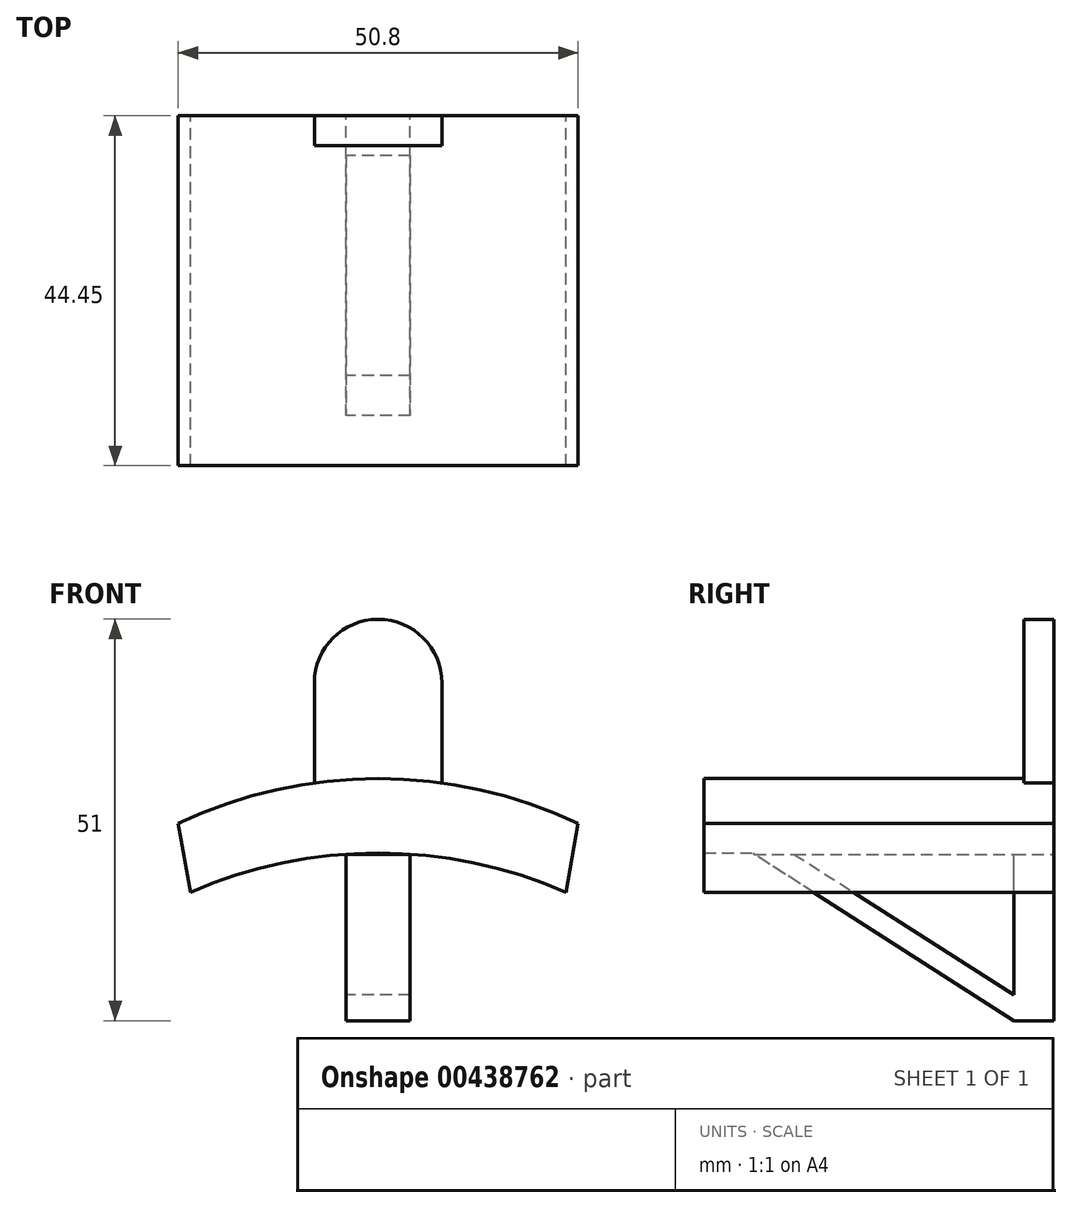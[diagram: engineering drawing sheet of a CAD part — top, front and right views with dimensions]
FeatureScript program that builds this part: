
annotation { "Feature Type Name" : "Feature", "Feature Type Description" : "" }
export const myFeature = defineFeature(function(context is Context, id is Id, definition is map)
    precondition{}
    {
        {
            var Q0;
            Q0=qCreatedBy(makeId("Front.planeOp"),FACE);
            var sketch = newSketch(context, id + "F0", { "sketchPlane" : qUnion([Q0])});
            skCircle(sketch, "E0", {"center": v(0, 0) * mm, "radius": 25.4 * mm, "construction": true});
            skArc(sketch, "E1", {"start": v(25.4, 0) * mm, "mid": v(0, 5.67) * mm, "end": v(-25.4, 0) * mm});
            skArc(sketch, "E2", {"start": v(23.84, -8.75) * mm, "mid": v(0, -3.78) * mm, "end": v(-23.84, -8.75) * mm});
            skLineSegment(sketch, "E3", {"start": v(-25.4, 0) * mm, "end": v(-23.84, -8.75) * mm});
            skLineSegment(sketch, "E4", {"start": v(25.4, 0) * mm, "end": v(23.84, -8.75) * mm});
            skLineSegment(sketch, "E5", {"start": v(-8.1, 5.12) * mm, "end": v(-8.1, 17.82) * mm});
            skLineSegment(sketch, "E6.MirrorCS", {"start": v(8.1, 5.12) * mm, "end": v(8.1, 17.82) * mm});
            skArc(sketch, "E7", {"start": v(8.1, 17.82) * mm, "mid": v(0, 25.93) * mm, "end": v(-8.1, 17.82) * mm});
            skLineSegment(sketch, "E8", {"start": v(-4.06, -3.92) * mm, "end": v(-4.06, -25.07) * mm});
            skLineSegment(sketch, "E9", {"start": v(-4.06, -25.07) * mm, "end": v(0, -25.07) * mm});
            skLineSegment(sketch, "E10.MirrorCS", {"start": v(4.06, -3.92) * mm, "end": v(4.06, -25.07) * mm});
            skLineSegment(sketch, "E11.MirrorCS", {"start": v(4.06, -25.07) * mm, "end": v(0, -25.07) * mm});
            skSolve(sketch);
        }
        {
            var Q0;
            {var subQ3=sQuery(id+"F0.wireOp",EDGE,"E3");Q0=makeQuery(id+"F0.imprint","IMPRINT",FACE,{"disambiguationData":[TD([[makeQuery(id+"F0.imprint","IMPRINT",EDGE,{"derivedFrom":subQ3}),1.0]])]});}
            extrude(context, id + "F1", {"entities" : qUnion([Q0]), "depth" : 44.45 * mm});
        }
        {
            var Q0;
            {var subQ0=sQuery(id+"F0.wireOp",EDGE,"E5");Q0=makeQuery(id+"F0.imprint","IMPRINT",FACE,{"disambiguationData":[TD([[makeQuery(id+"F0.imprint","IMPRINT",EDGE,{"derivedFrom":subQ0}),-1.0]])]});}
            extrude(context, id + "F2", {"entities" : qUnion([Q0]), "operationType" : NewBodyOperationType.ADD, "depth" : 3.8 * mm});
        }
        {
            var Q0;
            {var subQ1=sQuery(id+"F0.wireOp",EDGE,"E8");Q0=makeQuery(id+"F0.imprint","IMPRINT",FACE,{"disambiguationData":[TD([[makeQuery(id+"F0.imprint","IMPRINT",EDGE,{"derivedFrom":subQ1}),1.0]])]});}
            extrude(context, id + "F3", {"entities" : qUnion([Q0]), "operationType" : NewBodyOperationType.ADD, "depth" : 38.1 * mm});
        }
        {
            var Q0;
            Q0=makeQuery(id+"F3.opExtrude","SWEPT_FACE",FACE,{"disambiguationData":[OSD([sQuery(id+"F0.wireOp",EDGE,"E8")])]});
            var sketch = newSketch(context, id + "F4", { "sketchPlane" : qUnion([Q0])});
            skLineSegment(sketch, "E12", {"start": v(0, -3.92) * mm, "end": v(0, -25.07) * mm});
            skLineSegment(sketch, "E13", {"start": v(0, -25.07) * mm, "end": v(5.08, -25.07) * mm});
            skLineSegment(sketch, "E14", {"start": v(5.08, -25.07) * mm, "end": v(38.1, -3.92) * mm});
            skLineSegment(sketch, "E15", {"start": v(33.02, -3.92) * mm, "end": v(0, -25.07) * mm});
            skLineSegment(sketch, "E16", {"start": v(5.08, -25.07) * mm, "end": v(5.08, -3.92) * mm});
            skLineSegment(sketch, "E17", {"start": v(5.08, -3.92) * mm, "end": v(0, -3.92) * mm});
            skSolve(sketch);
        }
        {
            var Q0;
            {var subQ0=sQuery(id+"F4.wireOp",EDGE,"E15");var subQ3=sQuery(id+"F4.wireOp",EDGE,"E16");var subQ4=makeQuery(id+"F4.imprint","INTERSECT",VERTEX,{"derivedFrom":[subQ0,subQ3]});Q0=makeQuery(id+"F4.imprint","IMPRINT",FACE,{"disambiguationData":[TD([[makeQuery(id+"F4.imprint","IMPRINT",EDGE,{"disambiguationData":[TD([[subQ4,1.0]])],"derivedFrom":subQ0}),-1.0]])]});}
            var Q1;
            {var subQ0=sQuery(id+"F4.wireOp",EDGE,"E14");Q1=makeQuery(id+"F4.imprint","IMPRINT",FACE,{"disambiguationData":[TD([[makeQuery(id+"F4.imprint","IMPRINT",EDGE,{"derivedFrom":subQ0}),-1.0]])]});}
            extrude(context, id + "F5", {"entities" : qUnion([Q0, Q1]), "operationType" : NewBodyOperationType.REMOVE, "endBound" : BoundingType.UP_TO_NEXT, "oppositeDirection" : true, "depth" : 25.4 * mm});
        }
    });
